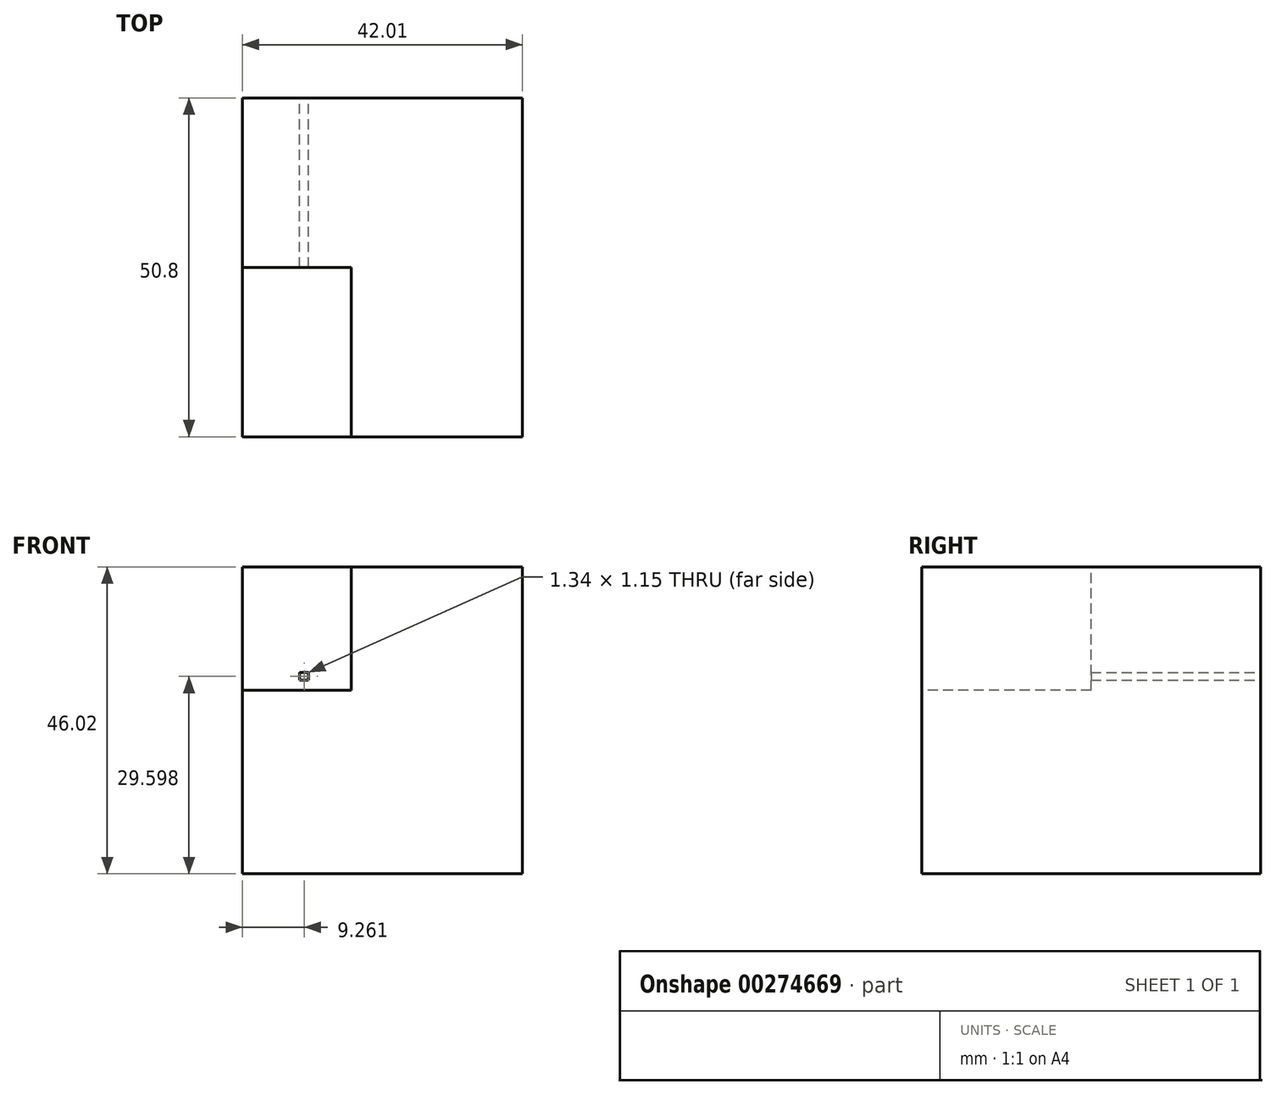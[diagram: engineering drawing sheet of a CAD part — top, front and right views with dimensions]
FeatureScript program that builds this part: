
annotation { "Feature Type Name" : "Feature", "Feature Type Description" : "" }
export const myFeature = defineFeature(function(context is Context, id is Id, definition is map)
    precondition{}
    {
        {
            var Q0;
            Q0=qCreatedBy(makeId("Front.planeOp"),FACE);
            var sketch = newSketch(context, id + "F0", { "sketchPlane" : qUnion([Q0])});
            skLineSegment(sketch, "E0.bottom", {"start": v(0, 0) * mm, "end": v(-42.01, 0) * mm});
            skLineSegment(sketch, "E0.top", {"start": v(0, 46.02) * mm, "end": v(-42.01, 46.02) * mm});
            skLineSegment(sketch, "E0.left", {"start": v(0, 0) * mm, "end": v(0, 46.02) * mm});
            skLineSegment(sketch, "E0.right", {"start": v(-42.01, 0) * mm, "end": v(-42.01, 46.02) * mm});
            skLineSegment(sketch, "E1.bottom", {"start": v(-33.42, 30.17) * mm, "end": v(-32.08, 30.17) * mm});
            skLineSegment(sketch, "E1.top", {"start": v(-33.42, 29.03) * mm, "end": v(-32.08, 29.03) * mm});
            skLineSegment(sketch, "E1.left", {"start": v(-33.42, 30.17) * mm, "end": v(-33.42, 29.03) * mm});
            skLineSegment(sketch, "E1.right", {"start": v(-32.08, 30.17) * mm, "end": v(-32.08, 29.03) * mm});
            skLineSegment(sketch, "E2.bottom", {"start": v(-42.01, 46.02) * mm, "end": v(-27.5, 46.02) * mm});
            skLineSegment(sketch, "E2.top", {"start": v(-42.01, 27.12) * mm, "end": v(-27.5, 27.12) * mm});
            skLineSegment(sketch, "E2.left", {"start": v(-42.01, 46.02) * mm, "end": v(-42.01, 27.12) * mm});
            skLineSegment(sketch, "E2.right", {"start": v(-27.5, 46.02) * mm, "end": v(-27.5, 27.12) * mm});
            skSolve(sketch);
        }
        {
            var Q0;
            Q0 = qSketchRegion(id + "F0", true);
            extrude(context, id + "F1", {"entities" : qUnion([Q0]), "depth" : 50.8 * mm});
        }
        {
            var Q0;
            Q0 = qSketchRegion(id + "F0", true);
            extrude(context, id + "F2", {"entities" : qUnion([Q0]), "operationType" : NewBodyOperationType.ADD, "depth" : 50.8 * mm});
        }
        {
            var Q0;
            Q0=makeQuery(id+"F1.opExtrude","CAP_FACE",FACE,{"disambiguationData":[OSD([sQuery(id+"F0.wireOp",EDGE,"E0.bottom"),sQuery(id+"F0.wireOp",EDGE,"E0.top"),sQuery(id+"F0.wireOp",EDGE,"E0.left"),sQuery(id+"F0.wireOp",EDGE,"E0.right"),sQuery(id+"F0.wireOp",EDGE,"E1.bottom"),sQuery(id+"F0.wireOp",EDGE,"E1.top"),sQuery(id+"F0.wireOp",EDGE,"E1.left"),sQuery(id+"F0.wireOp",EDGE,"E1.right"),sQuery(id+"F0.wireOp",EDGE,"E2.bottom"),sQuery(id+"F0.wireOp",EDGE,"E2.left")])],"isStart":false});
            var sketch = newSketch(context, id + "F3", { "sketchPlane" : qUnion([Q0])});
            skLineSegment(sketch, "E3.bottom", {"start": v(-51.06, 53.75) * mm, "end": v(-25.67, 53.75) * mm});
            skLineSegment(sketch, "E3.top", {"start": v(-51.06, 27.5) * mm, "end": v(-25.67, 27.5) * mm});
            skLineSegment(sketch, "E3.left", {"start": v(-51.06, 53.75) * mm, "end": v(-51.06, 27.5) * mm});
            skLineSegment(sketch, "E3.right", {"start": v(-25.67, 53.75) * mm, "end": v(-25.67, 27.5) * mm});
            skLineSegment(sketch, "E4.0.0", {"start": v(0, 46.02) * mm, "end": v(-42.01, 46.02) * mm});
            skLineSegment(sketch, "E4.0.2", {"start": v(-42.01, 46.02) * mm, "end": v(0, 46.02) * mm});
            skSolve(sketch);
        }
        {
            var Q0;
            Q0=makeQuery(id+"F3.imprint","IMPRINT",FACE,{"disambiguationData":[TD([[makeQuery(id+"F3.imprint","IMPRINT",EDGE,{"derivedFrom":makeQuery(id+"F1.opExtrude","CAP_EDGE",EDGE,{"disambiguationData":[OSD([sQuery(id+"F0.wireOp",EDGE,"E1.bottom")])],"isStart":false})}),1.0]])]});
            extrude(context, id + "F4", {"entities" : qUnion([Q0]), "operationType" : NewBodyOperationType.REMOVE, "oppositeDirection" : true, "depth" : 25.4 * mm});
        }
    });
